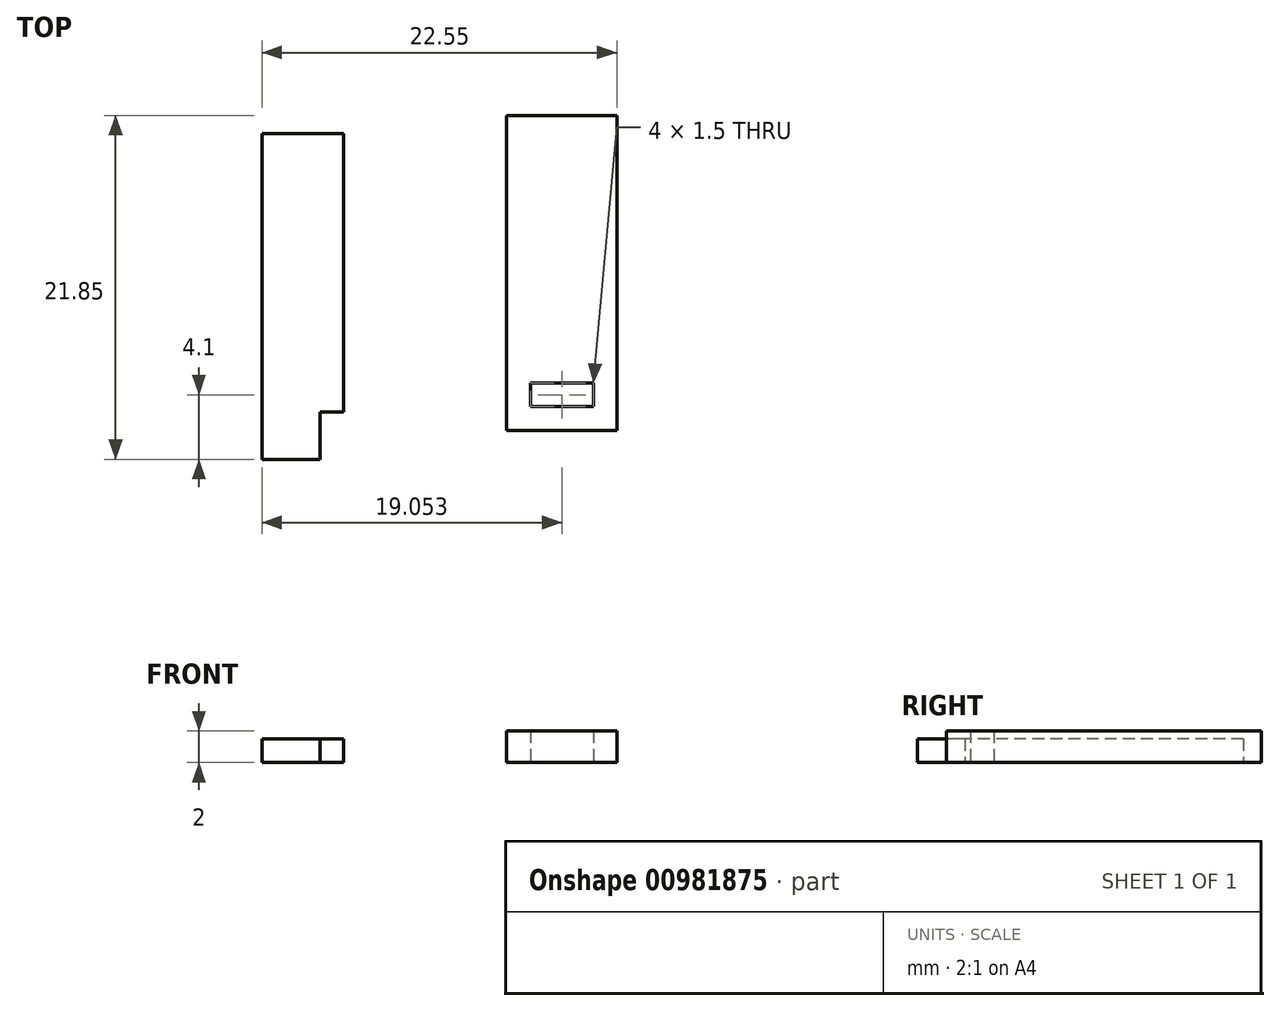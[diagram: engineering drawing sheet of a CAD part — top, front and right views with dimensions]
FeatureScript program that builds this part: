
annotation { "Feature Type Name" : "Feature", "Feature Type Description" : "" }
export const myFeature = defineFeature(function(context is Context, id is Id, definition is map)
    precondition{}
    {
        {
            var Q0;
            Q0=qCreatedBy(makeId("Top.planeOp"),FACE);
            var sketch = newSketch(context, id + "F0", { "sketchPlane" : qUnion([Q0])});
            skLineSegment(sketch, "E0.bottom", {"start": v(2.6, 8.85) * mm, "end": v(-2.6, 8.85) * mm});
            skLineSegment(sketch, "E0.top", {"start": v(2.6, -8.85) * mm, "end": v(-2.6, -8.85) * mm});
            skLineSegment(sketch, "E0.left", {"start": v(2.6, 8.85) * mm, "end": v(2.6, -8.85) * mm});
            skLineSegment(sketch, "E0.right", {"start": v(-2.6, 8.85) * mm, "end": v(-2.6, -8.85) * mm});
            skPoint(sketch, "E0.middle", {"position": v(0, 0) * mm});
            skLineSegment(sketch, "E1", {"start": v(-2.6, -8.85) * mm, "end": v(1.1, -8.85) * mm});
            skLineSegment(sketch, "E2", {"start": v(1.1, -8.85) * mm, "end": v(1.1, -11.85) * mm});
            skLineSegment(sketch, "E3", {"start": v(1.1, -11.85) * mm, "end": v(-2.6, -11.85) * mm});
            skLineSegment(sketch, "E4", {"start": v(-2.6, -11.85) * mm, "end": v(-2.6, -8.85) * mm});
            skSolve(sketch);
        }
        {
            var Q0;
            Q0=makeQuery(id+"F0.imprint","IMPRINT",FACE,{"disambiguationData":[TD([[makeQuery(id+"F0.imprint","IMPRINT",EDGE,{"derivedFrom":sQuery(id+"F0.wireOp",EDGE,"E0.bottom")}),1.0]])]});
            var Q1;
            {var subQ0=sQuery(id+"F0.wireOp",EDGE,"E2");Q1=makeQuery(id+"F0.imprint","IMPRINT",FACE,{"disambiguationData":[TD([[makeQuery(id+"F0.imprint","IMPRINT",EDGE,{"derivedFrom":subQ0}),-1.0]])]});}
            extrude(context, id + "F1", {"entities" : qUnion([Q0, Q1]), "depth" : 1.5 * mm, "offsetDistance" : 25 * mm});
        }
        {
            var Q0;
            Q0=qCreatedBy(makeId("Top.planeOp"),FACE);
            var sketch = newSketch(context, id + "F2", { "sketchPlane" : qUnion([Q0])});
            skLineSegment(sketch, "E5.bottom", {"start": v(19.95, -10) * mm, "end": v(12.95, -10) * mm});
            skLineSegment(sketch, "E5.top", {"start": v(19.95, 10) * mm, "end": v(12.95, 10) * mm});
            skLineSegment(sketch, "E5.left", {"start": v(19.95, -10) * mm, "end": v(19.95, 10) * mm});
            skLineSegment(sketch, "E5.right", {"start": v(12.95, -10) * mm, "end": v(12.95, 10) * mm});
            skPoint(sketch, "E5.middle", {"position": v(16.45, 0) * mm});
            skLineSegment(sketch, "E6", {"start": v(16.45, -10) * mm, "end": v(16.45, -8.5) * mm, "construction": true});
            skLineSegment(sketch, "E7", {"start": v(16.45, -8.5) * mm, "end": v(18.45, -8.5) * mm});
            skLineSegment(sketch, "E8", {"start": v(16.45, -8.5) * mm, "end": v(14.45, -8.5) * mm});
            skLineSegment(sketch, "E9", {"start": v(14.45, -8.5) * mm, "end": v(14.45, -7) * mm});
            skLineSegment(sketch, "E10", {"start": v(14.45, -7) * mm, "end": v(18.45, -7) * mm});
            skLineSegment(sketch, "E11", {"start": v(18.45, -8.5) * mm, "end": v(18.45, -7) * mm});
            skSolve(sketch);
        }
        {
            var Q0;
            Q0=makeQuery(id+"F2.imprint","IMPRINT",FACE,{"disambiguationData":[TD([[makeQuery(id+"F2.imprint","IMPRINT",EDGE,{"derivedFrom":sQuery(id+"F2.wireOp",EDGE,"E5.bottom")}),-1.0]])]});
            extrude(context, id + "F3", {"entities" : qUnion([Q0]), "depth" : 2 * mm, "offsetDistance" : 25 * mm});
        }
    });
